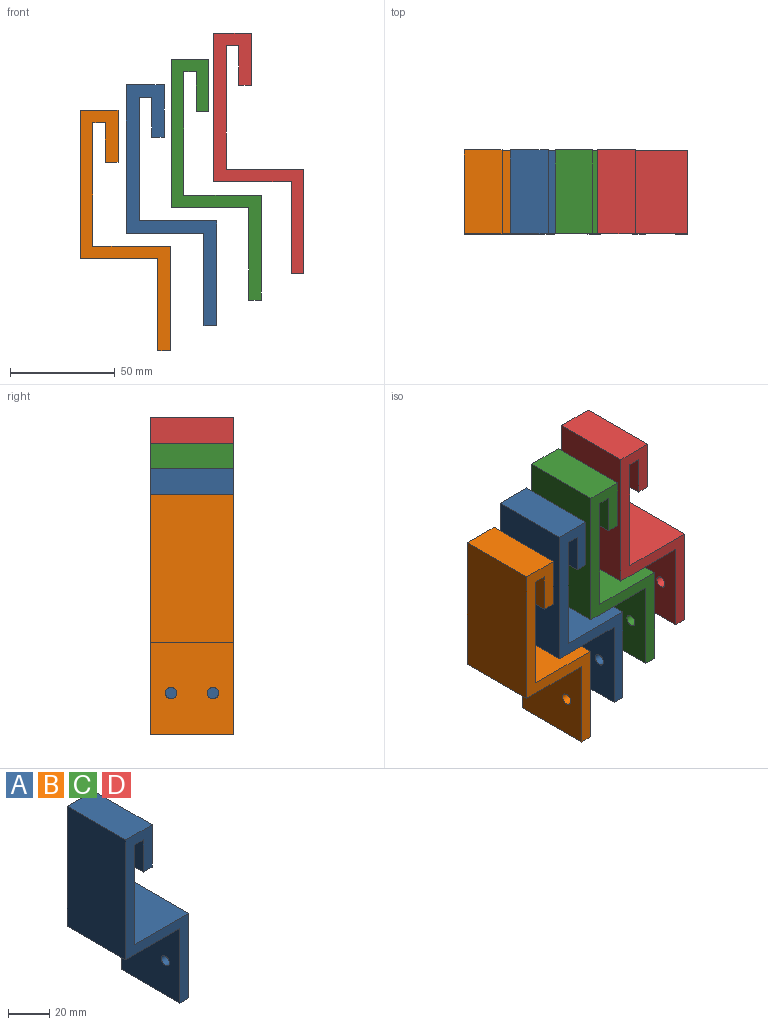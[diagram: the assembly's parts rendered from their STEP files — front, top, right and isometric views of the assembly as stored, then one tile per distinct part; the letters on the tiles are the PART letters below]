
ASSEMBLY  parts=4 mates=1
PART A: 16 faces, bbox 43x40x115 mm
  f0: plane 40x19mm, normal (-1,0,0), area 760mm2, adj f1,f11,f12,f13
  f1: plane 40x6mm, normal (0,0,-1), area 240mm2, adj f0,f2,f12,f13
  f2: plane 40x25mm, normal (1,0,0), area 1000mm2, adj f1,f3,f12,f13
  f3: plane 40x18mm, normal (0,0,1), area 720mm2, adj f2,f4,f12,f13
  f4: plane 71x40mm, normal (-1,0,0), area 2840mm2, adj f3,f5,f12,f13
  f5: plane 40x37mm, normal (0,0,-1), area 1480mm2, adj f4,f6,f12,f13
  f6: plane 44x40mm, normal (-1,0,0), area 1712.5mm2, adj f5,f7,f12,f13,f14,f15
  f7: plane 40x6mm, normal (0,0,-1), area 240mm2, adj f6,f8,f12,f13
  f8: plane 50x40mm, normal (1,0,0), area 1952.5mm2, adj f7,f9,f12,f13,f14,f15
  f9: plane 40x37mm, normal (0,0,1), area 1480mm2, adj f8,f10,f12,f13
  f10: plane 59x40mm, normal (1,0,0), area 2360mm2, adj f9,f11,f12,f13
  f11: plane 40x6mm, normal (0,0,-1), area 240mm2, adj f0,f10,f12,f13
  f12: plane 115x43mm, normal (0,-1,0), area 1098mm2, adj f0,f1,f2,f3,f4,f5,f6,f7
  f13: plane 115x43mm, normal (0,1,0), area 1098mm2, adj f0,f1,f2,f3,f4,f5,f6,f7
  f14: cylinder r=2.75mm len=6mm, axis (-1,0,0), area 103.7mm2, adj f6,f8
  f15: cylinder r=2.75mm len=6mm, axis (-1,0,0), area 103.7mm2, adj f6,f8
PART B: same geometry as A
PART C: same geometry as A
PART D: same geometry as A
PLACE A t=(43.16,20,24.51)mm
PLACE B t=(21.13,20,12.45)mm
PLACE C t=(64.53,20,36.76)mm
PLACE D t=(84.77,20,49.24)mm
MATE planar D.f12 <-> C.f12  axis (0,-1,0) through (90.85,-20,22.55)mm
